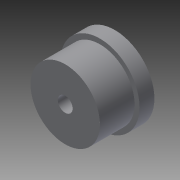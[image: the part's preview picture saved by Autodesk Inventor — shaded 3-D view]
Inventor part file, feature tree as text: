
AUTODESK INVENTOR PART (.ipt)
format: ipt  version: 2013 (Build 170138000, 138)  size: 88,576 bytes
history: native  units: mm
features: extrude x2, sketch x2, other x1
ambient origin geometry x8: Origin, YZ Plane, XZ Plane, XY Plane, X Axis, Y Axis, Z Axis, Center Point
feature tree (5):
  other  "ソリッド1"
  extrude  "押し出し1"  Depth=6.0mm
  extrude  "押し出し2"  Depth=28.0mm
  sketch  "スケッチ1"
  sketch  "スケッチ2"
